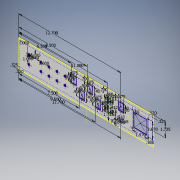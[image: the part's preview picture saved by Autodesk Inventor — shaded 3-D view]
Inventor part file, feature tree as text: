
AUTODESK INVENTOR PART (.ipt)
format: ipt  version: 2017 (Build 210142000, 142)  size: 296,448 bytes
history: native  units: in
note: dims shown in document units (in); Inventor stores cm internally (conversion verified against a paired STEP export)
features: extrude x7, other x6, hole x5, sketch x1, projected_geometry x1
ambient origin geometry x8: Origin, YZ Plane, XZ Plane, XY Plane, X Axis, Y Axis, Z Axis, Center Point
bodies: Solid1 (feature_tree)
feature tree (20):
  extrude  "Extrusion1"  Depth=3.47in
  other  "SMA"
  other  "airflow"
  other  "Dsub25"
  extrude  "sma cutouts"  Depth=0.065in TaperAngle=0.0deg
  hole  "dsub25 holes"  [1 undecoded]
  extrude  "dsub25 cutout"  Depth=1.0in
  other  "rj45"
  hole  "rj45 holes"  [1 undecoded]
  extrude  "rj45 cutouts"  Depth=1.0in
  other  "rj45 debug"
  hole  "rj45 debug holes"  [1 undecoded]
  extrude  "rj45 debug cutout"  Depth=1.0in
  other  "SC/SC"
  hole  "SC/SC holes"  [1 undecoded]
  extrude  "SC/SC cutout"  Depth=1.0in
  hole  "airflow holes"  [1 undecoded]
  extrude  "airflow cutout"  Depth=1.0in
  sketch  "Sketch1"  dims[d0=16.73in d1=3.47in d2=0.065in d3=0.0in d4=0.325in d5=0.12in d7=0.325in d8=0.12in d11=0.256in d12=0.236in d13=1.0in d14=1.0in d15=0.7874in d17=1.5in d18=0.7874in d20=1.0in d23=1.5748in d25=1.0in d26=0.3937in d28=1.0in d30=1.97in d31=1.97in d32=0.5in d46=1.857in d47=0.163in d48=0.163in d49=0.163in d50=0.163in d51=1.577in d52=1.452in d53=1.735in d57=0.46in d58=0.23in d59=11.0in d60=1.735in d63=1.0in d64=0.0in d147=0.116in d148=0.224in d149=0.375in d150=0.25in d151=0.5635in d152=0.349in d153=0.8108in d154=1.0in d155=0.0in d160=1.14in d161=0.9in d162=0.675in d163=6.5in d164=0.7in d165=1.14in d166=0.9in d167=0.675in d168=1.14in d169=0.9in d170=0.675in d171=1.14in d172=0.9in d173=0.675in d174=0.7in d175=8.5in d177=7.5in d179=9.5in d180=0.129in d181=0.224in d182=0.375in d183=0.25in d184=0.5635in d185=0.349in d186=0.8108in d187=1.0in d188=0.0in d189=1.14in d190=0.675in d191=0.9in d193=0.7in d194=12.7in d195=0.129in d196=0.224in d197=0.375in d198=0.25in d199=0.5635in d200=0.349in d201=0.8108in d202=1.0in d203=0.0in d204=0.51in d205=0.368in d206=0.7087in d207=12.7in d208=0.73in d209=0.094in d210=0.75in d211=0.217in d212=0.25in d213=90.0deg d214=1.0in d215=0.8108in d216=1.0in d217=0.0in d218=0.1549in d219=0.201in d220=0.75in d221=0.37in d222=0.25in d223=90.0deg d224=1.0in d225=0.8108in d226=1.0in d227=0.0in d229=1.735in]
  projected_geometry  "Projected Loop1"
note: 5 required parameter values undecoded (feature->parameter linkage not recoverable at this tier; creation-order binding heuristic only, values carry confidence <= 0.55)
